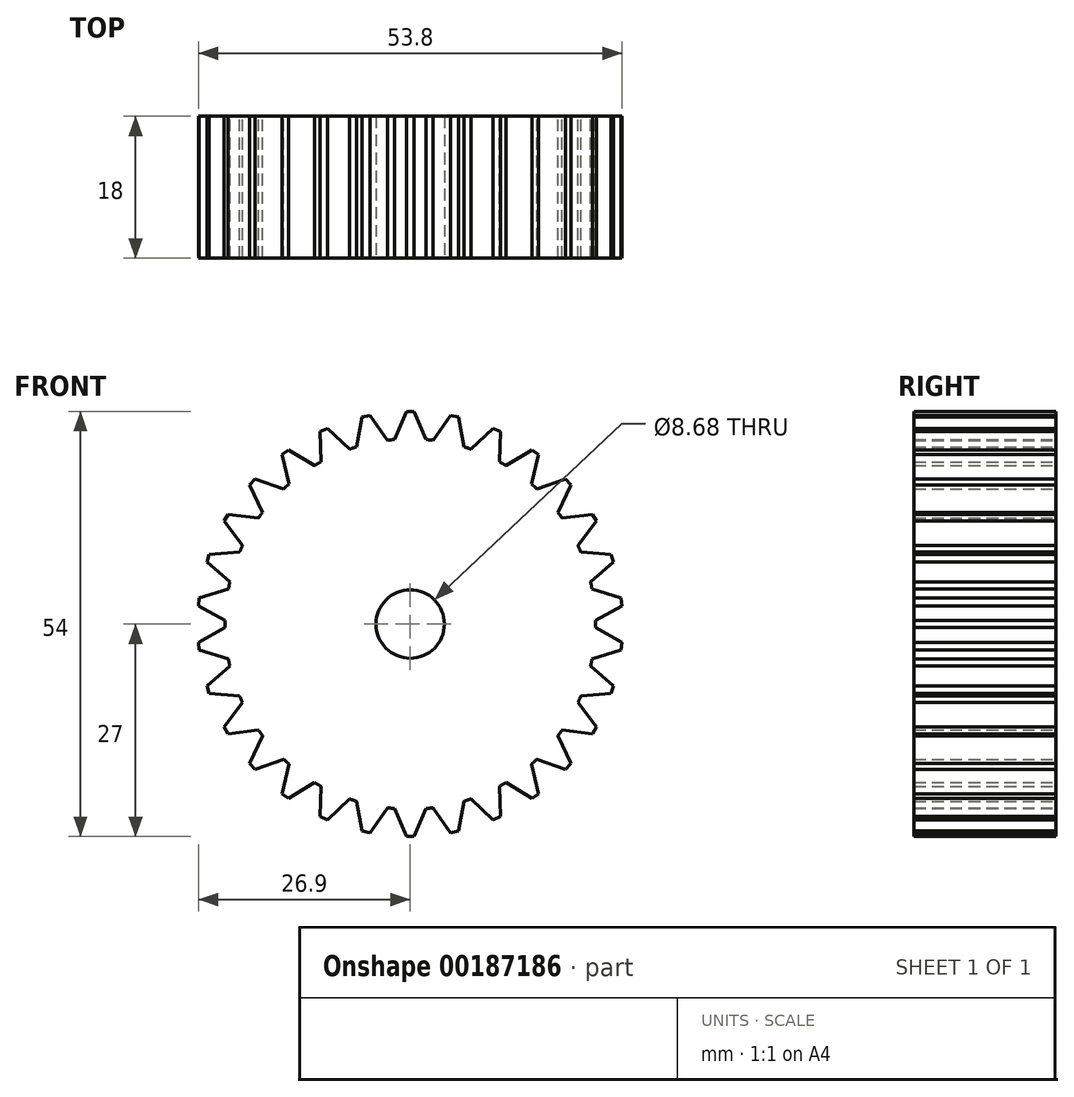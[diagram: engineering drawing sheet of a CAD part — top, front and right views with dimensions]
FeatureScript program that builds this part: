
annotation { "Feature Type Name" : "Feature", "Feature Type Description" : "" }
export const myFeature = defineFeature(function(context is Context, id is Id, definition is map)
    precondition{}
    {
        {
            var Q0;
            Q0=qCreatedBy(makeId("Front.planeOp"),FACE);
            var sketch = newSketch(context, id + "F0", { "sketchPlane" : qUnion([Q0])});
            skLineSegment(sketch, "E0", {"start": v(0, 0) * mm, "end": v(0, 27) * mm, "construction": true});
            skLineSegment(sketch, "E1", {"start": v(-0.5, 27) * mm, "end": v(0.5, 27) * mm, "construction": true});
            skLineSegment(sketch, "E2", {"start": v(0, 27) * mm, "end": v(0, 23.75) * mm, "construction": true});
            skPoint(sketch, "E3.startSnap0", {"position": v(0, 31.5) * mm});
            skLineSegment(sketch, "E4", {"start": v(-0.5, 27) * mm, "end": v(0, 27) * mm});
            skLineSegment(sketch, "E5.MirrorCS", {"start": v(0.5, 27) * mm, "end": v(0, 27) * mm});
            skLineSegment(sketch, "E6.MirrorCS", {"start": v(0.5, 27) * mm, "end": v(-0.5, 27) * mm, "construction": true});
            skCircle(sketch, "E7", {"center": v(0, 0) * mm, "radius": 23.52 * mm});
            skLineSegment(sketch, "E8", {"start": v(0.5, 27) * mm, "end": v(2, 23.44) * mm});
            skLineSegment(sketch, "E9", {"start": v(-0.5, 27) * mm, "end": v(-2, 23.44) * mm});
            skPoint(sketch, "E10.1.0", {"position": v(-6.55, 30.81) * mm});
            skLineSegment(sketch, "E10.1.1", {"start": v(-5.12, 26.51) * mm, "end": v(-2.92, 23.34) * mm});
            skLineSegment(sketch, "E10.1.2", {"start": v(-5.61, 26.4) * mm, "end": v(-4.94, 23.23) * mm, "construction": true});
            skLineSegment(sketch, "E10.1.3", {"start": v(-6.1, 26.3) * mm, "end": v(-6.83, 22.5) * mm});
            skPoint(sketch, "E10.1.4", {"position": v(-6.55, 30.81) * mm});
            skLineSegment(sketch, "E10.1.5", {"start": v(-5.12, 26.51) * mm, "end": v(-6.1, 26.3) * mm, "construction": true});
            skLineSegment(sketch, "E10.1.6", {"start": v(-6.1, 26.3) * mm, "end": v(-5.12, 26.51) * mm, "construction": true});
            skLineSegment(sketch, "E10.1.7", {"start": v(-5.12, 26.51) * mm, "end": v(-5.61, 26.4) * mm});
            skLineSegment(sketch, "E10.1.8", {"start": v(-6.1, 26.3) * mm, "end": v(-5.61, 26.4) * mm});
            skPoint(sketch, "E10.2.0", {"position": v(-12.81, 28.78) * mm});
            skLineSegment(sketch, "E10.2.1", {"start": v(-10.53, 24.87) * mm, "end": v(-7.7, 22.22) * mm});
            skLineSegment(sketch, "E10.2.2", {"start": v(-10.98, 24.67) * mm, "end": v(-9.66, 21.7) * mm, "construction": true});
            skLineSegment(sketch, "E10.2.3", {"start": v(-11.44, 24.46) * mm, "end": v(-11.36, 20.6) * mm});
            skPoint(sketch, "E10.2.4", {"position": v(-12.81, 28.78) * mm});
            skLineSegment(sketch, "E10.2.5", {"start": v(-10.53, 24.87) * mm, "end": v(-11.44, 24.46) * mm, "construction": true});
            skLineSegment(sketch, "E10.2.6", {"start": v(-11.44, 24.46) * mm, "end": v(-10.53, 24.87) * mm, "construction": true});
            skLineSegment(sketch, "E10.2.7", {"start": v(-10.53, 24.87) * mm, "end": v(-10.98, 24.67) * mm});
            skLineSegment(sketch, "E10.2.8", {"start": v(-11.44, 24.46) * mm, "end": v(-10.98, 24.67) * mm});
            skPoint(sketch, "E10.3.0", {"position": v(-18.52, 25.48) * mm});
            skLineSegment(sketch, "E10.3.1", {"start": v(-15.47, 22.14) * mm, "end": v(-12.16, 20.14) * mm});
            skLineSegment(sketch, "E10.3.2", {"start": v(-15.87, 21.84) * mm, "end": v(-13.96, 19.21) * mm, "construction": true});
            skLineSegment(sketch, "E10.3.3", {"start": v(-16.27, 21.55) * mm, "end": v(-15.4, 17.79) * mm});
            skPoint(sketch, "E10.3.4", {"position": v(-18.52, 25.48) * mm});
            skLineSegment(sketch, "E10.3.5", {"start": v(-15.47, 22.14) * mm, "end": v(-16.27, 21.55) * mm, "construction": true});
            skLineSegment(sketch, "E10.3.6", {"start": v(-16.27, 21.55) * mm, "end": v(-15.47, 22.14) * mm, "construction": true});
            skLineSegment(sketch, "E10.3.7", {"start": v(-15.47, 22.14) * mm, "end": v(-15.87, 21.84) * mm});
            skLineSegment(sketch, "E10.3.8", {"start": v(-16.27, 21.55) * mm, "end": v(-15.87, 21.84) * mm});
            skPoint(sketch, "E10.4.0", {"position": v(-23.4, 21.08) * mm});
            skLineSegment(sketch, "E10.4.1", {"start": v(-19.73, 18.44) * mm, "end": v(-16.08, 17.17) * mm});
            skLineSegment(sketch, "E10.4.2", {"start": v(-20.06, 18.07) * mm, "end": v(-17.65, 15.9) * mm, "construction": true});
            skLineSegment(sketch, "E10.4.3", {"start": v(-20.4, 17.7) * mm, "end": v(-18.76, 14.2) * mm});
            skPoint(sketch, "E10.4.4", {"position": v(-23.4, 21.08) * mm});
            skLineSegment(sketch, "E10.4.5", {"start": v(-19.73, 18.44) * mm, "end": v(-20.4, 17.7) * mm, "construction": true});
            skLineSegment(sketch, "E10.4.6", {"start": v(-20.4, 17.7) * mm, "end": v(-19.73, 18.44) * mm, "construction": true});
            skLineSegment(sketch, "E10.4.7", {"start": v(-19.73, 18.44) * mm, "end": v(-20.06, 18.07) * mm});
            skLineSegment(sketch, "E10.4.8", {"start": v(-20.4, 17.7) * mm, "end": v(-20.06, 18.07) * mm});
            skPoint(sketch, "E10.5.0", {"position": v(-27.28, 15.75) * mm});
            skLineSegment(sketch, "E10.5.1", {"start": v(-23.13, 13.93) * mm, "end": v(-19.3, 13.45) * mm});
            skLineSegment(sketch, "E10.5.2", {"start": v(-23.38, 13.5) * mm, "end": v(-20.57, 11.88) * mm, "construction": true});
            skLineSegment(sketch, "E10.5.3", {"start": v(-23.63, 13.07) * mm, "end": v(-21.3, 9.99) * mm});
            skPoint(sketch, "E10.5.4", {"position": v(-27.28, 15.75) * mm});
            skLineSegment(sketch, "E10.5.5", {"start": v(-23.13, 13.93) * mm, "end": v(-23.63, 13.07) * mm, "construction": true});
            skLineSegment(sketch, "E10.5.6", {"start": v(-23.63, 13.07) * mm, "end": v(-23.13, 13.93) * mm, "construction": true});
            skLineSegment(sketch, "E10.5.7", {"start": v(-23.13, 13.93) * mm, "end": v(-23.38, 13.5) * mm});
            skLineSegment(sketch, "E10.5.8", {"start": v(-23.63, 13.07) * mm, "end": v(-23.38, 13.5) * mm});
            skPoint(sketch, "E10.6.0", {"position": v(-29.96, 9.73) * mm});
            skLineSegment(sketch, "E10.6.1", {"start": v(-25.52, 8.82) * mm, "end": v(-21.67, 9.14) * mm});
            skLineSegment(sketch, "E10.6.2", {"start": v(-25.68, 8.34) * mm, "end": v(-22.59, 7.34) * mm, "construction": true});
            skLineSegment(sketch, "E10.6.3", {"start": v(-25.83, 7.87) * mm, "end": v(-22.9, 5.34) * mm});
            skPoint(sketch, "E10.6.4", {"position": v(-29.96, 9.73) * mm});
            skLineSegment(sketch, "E10.6.5", {"start": v(-25.52, 8.82) * mm, "end": v(-25.83, 7.87) * mm, "construction": true});
            skLineSegment(sketch, "E10.6.6", {"start": v(-25.83, 7.87) * mm, "end": v(-25.52, 8.82) * mm, "construction": true});
            skLineSegment(sketch, "E10.6.7", {"start": v(-25.52, 8.82) * mm, "end": v(-25.68, 8.34) * mm});
            skLineSegment(sketch, "E10.6.8", {"start": v(-25.83, 7.87) * mm, "end": v(-25.68, 8.34) * mm});
            skPoint(sketch, "E10.7.0", {"position": v(-31.33, 3.3) * mm});
            skLineSegment(sketch, "E10.7.1", {"start": v(-26.8, 3.32) * mm, "end": v(-23.1, 4.44) * mm});
            skLineSegment(sketch, "E10.7.2", {"start": v(-26.85, 2.82) * mm, "end": v(-23.62, 2.48) * mm, "construction": true});
            skLineSegment(sketch, "E10.7.3", {"start": v(-26.9, 2.33) * mm, "end": v(-23.52, 0.46) * mm});
            skPoint(sketch, "E10.7.4", {"position": v(-31.33, 3.3) * mm});
            skLineSegment(sketch, "E10.7.5", {"start": v(-26.8, 3.32) * mm, "end": v(-26.9, 2.33) * mm, "construction": true});
            skLineSegment(sketch, "E10.7.6", {"start": v(-26.9, 2.33) * mm, "end": v(-26.8, 3.32) * mm, "construction": true});
            skLineSegment(sketch, "E10.7.7", {"start": v(-26.8, 3.32) * mm, "end": v(-26.85, 2.82) * mm});
            skLineSegment(sketch, "E10.7.8", {"start": v(-26.9, 2.33) * mm, "end": v(-26.85, 2.82) * mm});
            skPoint(sketch, "E10.8.0", {"position": v(-31.33, -3.3) * mm});
            skLineSegment(sketch, "E10.8.1", {"start": v(-26.9, -2.33) * mm, "end": v(-23.52, -0.46) * mm});
            skLineSegment(sketch, "E10.8.2", {"start": v(-26.85, -2.82) * mm, "end": v(-23.62, -2.48) * mm, "construction": true});
            skLineSegment(sketch, "E10.8.3", {"start": v(-26.8, -3.32) * mm, "end": v(-23.1, -4.44) * mm});
            skPoint(sketch, "E10.8.4", {"position": v(-31.33, -3.3) * mm});
            skLineSegment(sketch, "E10.8.5", {"start": v(-26.9, -2.33) * mm, "end": v(-26.8, -3.32) * mm, "construction": true});
            skLineSegment(sketch, "E10.8.6", {"start": v(-26.8, -3.32) * mm, "end": v(-26.9, -2.33) * mm, "construction": true});
            skLineSegment(sketch, "E10.8.7", {"start": v(-26.9, -2.33) * mm, "end": v(-26.85, -2.82) * mm});
            skLineSegment(sketch, "E10.8.8", {"start": v(-26.8, -3.32) * mm, "end": v(-26.85, -2.82) * mm});
            skPoint(sketch, "E10.9.0", {"position": v(-29.96, -9.73) * mm});
            skLineSegment(sketch, "E10.9.1", {"start": v(-25.83, -7.87) * mm, "end": v(-22.9, -5.34) * mm});
            skLineSegment(sketch, "E10.9.2", {"start": v(-25.68, -8.34) * mm, "end": v(-22.59, -7.34) * mm, "construction": true});
            skLineSegment(sketch, "E10.9.3", {"start": v(-25.52, -8.82) * mm, "end": v(-21.67, -9.14) * mm});
            skPoint(sketch, "E10.9.4", {"position": v(-29.96, -9.73) * mm});
            skLineSegment(sketch, "E10.9.5", {"start": v(-25.83, -7.87) * mm, "end": v(-25.52, -8.82) * mm, "construction": true});
            skLineSegment(sketch, "E10.9.6", {"start": v(-25.52, -8.82) * mm, "end": v(-25.83, -7.87) * mm, "construction": true});
            skLineSegment(sketch, "E10.9.7", {"start": v(-25.83, -7.87) * mm, "end": v(-25.68, -8.34) * mm});
            skLineSegment(sketch, "E10.9.8", {"start": v(-25.52, -8.82) * mm, "end": v(-25.68, -8.34) * mm});
            skPoint(sketch, "E10.10.0", {"position": v(-27.28, -15.75) * mm});
            skLineSegment(sketch, "E10.10.1", {"start": v(-23.63, -13.07) * mm, "end": v(-21.3, -9.99) * mm});
            skLineSegment(sketch, "E10.10.2", {"start": v(-23.38, -13.5) * mm, "end": v(-20.57, -11.87) * mm, "construction": true});
            skLineSegment(sketch, "E10.10.3", {"start": v(-23.13, -13.93) * mm, "end": v(-19.3, -13.45) * mm});
            skPoint(sketch, "E10.10.4", {"position": v(-27.28, -15.75) * mm});
            skLineSegment(sketch, "E10.10.5", {"start": v(-23.63, -13.07) * mm, "end": v(-23.13, -13.93) * mm, "construction": true});
            skLineSegment(sketch, "E10.10.6", {"start": v(-23.13, -13.93) * mm, "end": v(-23.63, -13.07) * mm, "construction": true});
            skLineSegment(sketch, "E10.10.7", {"start": v(-23.63, -13.07) * mm, "end": v(-23.38, -13.5) * mm});
            skLineSegment(sketch, "E10.10.8", {"start": v(-23.13, -13.93) * mm, "end": v(-23.38, -13.5) * mm});
            skPoint(sketch, "E10.11.0", {"position": v(-23.4, -21.08) * mm});
            skLineSegment(sketch, "E10.11.1", {"start": v(-20.4, -17.7) * mm, "end": v(-18.76, -14.2) * mm});
            skLineSegment(sketch, "E10.11.2", {"start": v(-20.06, -18.07) * mm, "end": v(-17.65, -15.9) * mm, "construction": true});
            skLineSegment(sketch, "E10.11.3", {"start": v(-19.73, -18.44) * mm, "end": v(-16.08, -17.17) * mm});
            skPoint(sketch, "E10.11.4", {"position": v(-23.4, -21.08) * mm});
            skLineSegment(sketch, "E10.11.5", {"start": v(-20.4, -17.7) * mm, "end": v(-19.73, -18.44) * mm, "construction": true});
            skLineSegment(sketch, "E10.11.6", {"start": v(-19.73, -18.44) * mm, "end": v(-20.4, -17.7) * mm, "construction": true});
            skLineSegment(sketch, "E10.11.7", {"start": v(-20.4, -17.7) * mm, "end": v(-20.06, -18.07) * mm});
            skLineSegment(sketch, "E10.11.8", {"start": v(-19.73, -18.44) * mm, "end": v(-20.06, -18.07) * mm});
            skLineSegment(sketch, "E11.1.12.0", {"start": v(-16.27, -21.55) * mm, "end": v(-15.4, -17.79) * mm});
            skLineSegment(sketch, "E11.4.12.0", {"start": v(-15.87, -21.84) * mm, "end": v(-13.96, -19.21) * mm, "construction": true});
            skLineSegment(sketch, "E11.7.12.0", {"start": v(-15.47, -22.14) * mm, "end": v(-12.16, -20.14) * mm});
            skPoint(sketch, "E11.9.12.0", {"position": v(-18.52, -25.48) * mm});
            skPoint(sketch, "E11.10.12.0", {"position": v(-18.52, -25.48) * mm});
            skLineSegment(sketch, "E11.11.12.0", {"start": v(-16.27, -21.55) * mm, "end": v(-15.47, -22.14) * mm, "construction": true});
            skLineSegment(sketch, "E11.14.12.0", {"start": v(-15.47, -22.14) * mm, "end": v(-16.27, -21.55) * mm, "construction": true});
            skLineSegment(sketch, "E11.17.12.0", {"start": v(-16.27, -21.55) * mm, "end": v(-15.87, -21.84) * mm});
            skLineSegment(sketch, "E11.20.12.0", {"start": v(-15.47, -22.14) * mm, "end": v(-15.87, -21.84) * mm});
            skLineSegment(sketch, "E11.1.13.0", {"start": v(-11.44, -24.46) * mm, "end": v(-11.36, -20.6) * mm});
            skLineSegment(sketch, "E11.4.13.0", {"start": v(-10.98, -24.67) * mm, "end": v(-9.66, -21.7) * mm, "construction": true});
            skLineSegment(sketch, "E11.7.13.0", {"start": v(-10.53, -24.87) * mm, "end": v(-7.7, -22.22) * mm});
            skPoint(sketch, "E11.9.13.0", {"position": v(-12.81, -28.78) * mm});
            skPoint(sketch, "E11.10.13.0", {"position": v(-12.81, -28.78) * mm});
            skLineSegment(sketch, "E11.11.13.0", {"start": v(-11.44, -24.46) * mm, "end": v(-10.53, -24.87) * mm, "construction": true});
            skLineSegment(sketch, "E11.14.13.0", {"start": v(-10.53, -24.87) * mm, "end": v(-11.44, -24.46) * mm, "construction": true});
            skLineSegment(sketch, "E11.17.13.0", {"start": v(-11.44, -24.46) * mm, "end": v(-10.98, -24.67) * mm});
            skLineSegment(sketch, "E11.20.13.0", {"start": v(-10.53, -24.87) * mm, "end": v(-10.98, -24.67) * mm});
            skLineSegment(sketch, "E11.1.14.0", {"start": v(-6.1, -26.3) * mm, "end": v(-6.83, -22.5) * mm});
            skLineSegment(sketch, "E11.4.14.0", {"start": v(-5.61, -26.4) * mm, "end": v(-4.94, -23.23) * mm, "construction": true});
            skLineSegment(sketch, "E11.7.14.0", {"start": v(-5.12, -26.51) * mm, "end": v(-2.92, -23.34) * mm});
            skPoint(sketch, "E11.9.14.0", {"position": v(-6.55, -30.81) * mm});
            skPoint(sketch, "E11.10.14.0", {"position": v(-6.55, -30.81) * mm});
            skLineSegment(sketch, "E11.11.14.0", {"start": v(-6.1, -26.3) * mm, "end": v(-5.12, -26.51) * mm, "construction": true});
            skLineSegment(sketch, "E11.14.14.0", {"start": v(-5.12, -26.51) * mm, "end": v(-6.1, -26.3) * mm, "construction": true});
            skLineSegment(sketch, "E11.17.14.0", {"start": v(-6.1, -26.3) * mm, "end": v(-5.61, -26.4) * mm});
            skLineSegment(sketch, "E11.20.14.0", {"start": v(-5.12, -26.51) * mm, "end": v(-5.61, -26.4) * mm});
            skLineSegment(sketch, "E11.1.15.0", {"start": v(-0.5, -27) * mm, "end": v(-2, -23.44) * mm});
            skLineSegment(sketch, "E11.4.15.0", {"start": v(0, -27) * mm, "end": v(0, -23.75) * mm, "construction": true});
            skLineSegment(sketch, "E11.7.15.0", {"start": v(0.5, -27) * mm, "end": v(2, -23.44) * mm});
            skPoint(sketch, "E11.9.15.0", {"position": v(0, -31.5) * mm});
            skPoint(sketch, "E11.10.15.0", {"position": v(0, -31.5) * mm});
            skLineSegment(sketch, "E11.11.15.0", {"start": v(-0.5, -27) * mm, "end": v(0.5, -27) * mm, "construction": true});
            skLineSegment(sketch, "E11.14.15.0", {"start": v(0.5, -27) * mm, "end": v(-0.5, -27) * mm, "construction": true});
            skLineSegment(sketch, "E11.17.15.0", {"start": v(-0.5, -27) * mm, "end": v(0, -27) * mm});
            skLineSegment(sketch, "E11.20.15.0", {"start": v(0.5, -27) * mm, "end": v(0, -27) * mm});
            skLineSegment(sketch, "E11.1.16.0", {"start": v(5.12, -26.51) * mm, "end": v(2.92, -23.34) * mm});
            skLineSegment(sketch, "E11.4.16.0", {"start": v(5.61, -26.4) * mm, "end": v(4.94, -23.23) * mm, "construction": true});
            skLineSegment(sketch, "E11.7.16.0", {"start": v(6.1, -26.3) * mm, "end": v(6.83, -22.5) * mm});
            skPoint(sketch, "E11.9.16.0", {"position": v(6.55, -30.81) * mm});
            skPoint(sketch, "E11.10.16.0", {"position": v(6.55, -30.81) * mm});
            skLineSegment(sketch, "E11.11.16.0", {"start": v(5.12, -26.51) * mm, "end": v(6.1, -26.3) * mm, "construction": true});
            skLineSegment(sketch, "E11.14.16.0", {"start": v(6.1, -26.3) * mm, "end": v(5.12, -26.51) * mm, "construction": true});
            skLineSegment(sketch, "E11.17.16.0", {"start": v(5.12, -26.51) * mm, "end": v(5.61, -26.4) * mm});
            skLineSegment(sketch, "E11.20.16.0", {"start": v(6.1, -26.3) * mm, "end": v(5.61, -26.4) * mm});
            skLineSegment(sketch, "E11.1.17.0", {"start": v(10.53, -24.87) * mm, "end": v(7.7, -22.22) * mm});
            skLineSegment(sketch, "E11.4.17.0", {"start": v(10.98, -24.67) * mm, "end": v(9.66, -21.7) * mm, "construction": true});
            skLineSegment(sketch, "E11.7.17.0", {"start": v(11.44, -24.46) * mm, "end": v(11.36, -20.6) * mm});
            skPoint(sketch, "E11.9.17.0", {"position": v(12.81, -28.78) * mm});
            skPoint(sketch, "E11.10.17.0", {"position": v(12.81, -28.78) * mm});
            skLineSegment(sketch, "E11.11.17.0", {"start": v(10.53, -24.87) * mm, "end": v(11.44, -24.46) * mm, "construction": true});
            skLineSegment(sketch, "E11.14.17.0", {"start": v(11.44, -24.46) * mm, "end": v(10.53, -24.87) * mm, "construction": true});
            skLineSegment(sketch, "E11.17.17.0", {"start": v(10.53, -24.87) * mm, "end": v(10.98, -24.67) * mm});
            skLineSegment(sketch, "E11.20.17.0", {"start": v(11.44, -24.46) * mm, "end": v(10.98, -24.67) * mm});
            skLineSegment(sketch, "E11.1.18.0", {"start": v(15.47, -22.14) * mm, "end": v(12.16, -20.14) * mm});
            skLineSegment(sketch, "E11.4.18.0", {"start": v(15.87, -21.84) * mm, "end": v(13.96, -19.21) * mm, "construction": true});
            skLineSegment(sketch, "E11.7.18.0", {"start": v(16.27, -21.55) * mm, "end": v(15.4, -17.79) * mm});
            skPoint(sketch, "E11.9.18.0", {"position": v(18.52, -25.48) * mm});
            skPoint(sketch, "E11.10.18.0", {"position": v(18.52, -25.48) * mm});
            skLineSegment(sketch, "E11.11.18.0", {"start": v(15.47, -22.14) * mm, "end": v(16.27, -21.55) * mm, "construction": true});
            skLineSegment(sketch, "E11.14.18.0", {"start": v(16.27, -21.55) * mm, "end": v(15.47, -22.14) * mm, "construction": true});
            skLineSegment(sketch, "E11.17.18.0", {"start": v(15.47, -22.14) * mm, "end": v(15.87, -21.84) * mm});
            skLineSegment(sketch, "E11.20.18.0", {"start": v(16.27, -21.55) * mm, "end": v(15.87, -21.84) * mm});
            skLineSegment(sketch, "E11.1.19.0", {"start": v(19.73, -18.44) * mm, "end": v(16.08, -17.17) * mm});
            skLineSegment(sketch, "E11.4.19.0", {"start": v(20.06, -18.07) * mm, "end": v(17.65, -15.9) * mm, "construction": true});
            skLineSegment(sketch, "E11.7.19.0", {"start": v(20.4, -17.7) * mm, "end": v(18.76, -14.2) * mm});
            skPoint(sketch, "E11.9.19.0", {"position": v(23.4, -21.08) * mm});
            skPoint(sketch, "E11.10.19.0", {"position": v(23.4, -21.08) * mm});
            skLineSegment(sketch, "E11.11.19.0", {"start": v(19.73, -18.44) * mm, "end": v(20.4, -17.7) * mm, "construction": true});
            skLineSegment(sketch, "E11.14.19.0", {"start": v(20.4, -17.7) * mm, "end": v(19.73, -18.44) * mm, "construction": true});
            skLineSegment(sketch, "E11.17.19.0", {"start": v(19.73, -18.44) * mm, "end": v(20.06, -18.07) * mm});
            skLineSegment(sketch, "E11.20.19.0", {"start": v(20.4, -17.7) * mm, "end": v(20.06, -18.07) * mm});
            skLineSegment(sketch, "E12.1.20.0", {"start": v(23.13, -13.93) * mm, "end": v(19.3, -13.45) * mm});
            skLineSegment(sketch, "E12.4.20.0", {"start": v(23.38, -13.5) * mm, "end": v(20.57, -11.88) * mm, "construction": true});
            skLineSegment(sketch, "E12.7.20.0", {"start": v(23.63, -13.07) * mm, "end": v(21.3, -9.99) * mm});
            skPoint(sketch, "E12.9.20.0", {"position": v(27.28, -15.75) * mm});
            skPoint(sketch, "E12.10.20.0", {"position": v(27.28, -15.75) * mm});
            skLineSegment(sketch, "E12.11.20.0", {"start": v(23.13, -13.93) * mm, "end": v(23.63, -13.07) * mm, "construction": true});
            skLineSegment(sketch, "E12.14.20.0", {"start": v(23.63, -13.07) * mm, "end": v(23.13, -13.93) * mm, "construction": true});
            skLineSegment(sketch, "E12.17.20.0", {"start": v(23.13, -13.93) * mm, "end": v(23.38, -13.5) * mm});
            skLineSegment(sketch, "E12.20.20.0", {"start": v(23.63, -13.07) * mm, "end": v(23.38, -13.5) * mm});
            skLineSegment(sketch, "E12.1.21.0", {"start": v(25.52, -8.82) * mm, "end": v(21.67, -9.14) * mm});
            skLineSegment(sketch, "E12.4.21.0", {"start": v(25.68, -8.34) * mm, "end": v(22.59, -7.34) * mm, "construction": true});
            skLineSegment(sketch, "E12.7.21.0", {"start": v(25.83, -7.87) * mm, "end": v(22.9, -5.34) * mm});
            skPoint(sketch, "E12.9.21.0", {"position": v(29.96, -9.73) * mm});
            skPoint(sketch, "E12.10.21.0", {"position": v(29.96, -9.73) * mm});
            skLineSegment(sketch, "E12.11.21.0", {"start": v(25.52, -8.82) * mm, "end": v(25.83, -7.87) * mm, "construction": true});
            skLineSegment(sketch, "E12.14.21.0", {"start": v(25.83, -7.87) * mm, "end": v(25.52, -8.82) * mm, "construction": true});
            skLineSegment(sketch, "E12.17.21.0", {"start": v(25.52, -8.82) * mm, "end": v(25.68, -8.34) * mm});
            skLineSegment(sketch, "E12.20.21.0", {"start": v(25.83, -7.87) * mm, "end": v(25.68, -8.34) * mm});
            skLineSegment(sketch, "E12.1.22.0", {"start": v(26.8, -3.32) * mm, "end": v(23.1, -4.44) * mm});
            skLineSegment(sketch, "E12.4.22.0", {"start": v(26.85, -2.82) * mm, "end": v(23.62, -2.48) * mm, "construction": true});
            skLineSegment(sketch, "E12.7.22.0", {"start": v(26.9, -2.33) * mm, "end": v(23.52, -0.46) * mm});
            skPoint(sketch, "E12.9.22.0", {"position": v(31.33, -3.3) * mm});
            skPoint(sketch, "E12.10.22.0", {"position": v(31.33, -3.3) * mm});
            skLineSegment(sketch, "E12.11.22.0", {"start": v(26.8, -3.32) * mm, "end": v(26.9, -2.33) * mm, "construction": true});
            skLineSegment(sketch, "E12.14.22.0", {"start": v(26.9, -2.33) * mm, "end": v(26.8, -3.32) * mm, "construction": true});
            skLineSegment(sketch, "E12.17.22.0", {"start": v(26.8, -3.32) * mm, "end": v(26.85, -2.82) * mm});
            skLineSegment(sketch, "E12.20.22.0", {"start": v(26.9, -2.33) * mm, "end": v(26.85, -2.82) * mm});
            skLineSegment(sketch, "E12.1.23.0", {"start": v(26.9, 2.33) * mm, "end": v(23.52, 0.46) * mm});
            skLineSegment(sketch, "E12.4.23.0", {"start": v(26.85, 2.82) * mm, "end": v(23.62, 2.48) * mm, "construction": true});
            skLineSegment(sketch, "E12.7.23.0", {"start": v(26.8, 3.32) * mm, "end": v(23.1, 4.44) * mm});
            skPoint(sketch, "E12.9.23.0", {"position": v(31.33, 3.3) * mm});
            skPoint(sketch, "E12.10.23.0", {"position": v(31.33, 3.3) * mm});
            skLineSegment(sketch, "E12.11.23.0", {"start": v(26.9, 2.33) * mm, "end": v(26.8, 3.32) * mm, "construction": true});
            skLineSegment(sketch, "E12.14.23.0", {"start": v(26.8, 3.32) * mm, "end": v(26.9, 2.33) * mm, "construction": true});
            skLineSegment(sketch, "E12.17.23.0", {"start": v(26.9, 2.33) * mm, "end": v(26.85, 2.82) * mm});
            skLineSegment(sketch, "E12.20.23.0", {"start": v(26.8, 3.32) * mm, "end": v(26.85, 2.82) * mm});
            skLineSegment(sketch, "E12.1.24.0", {"start": v(25.83, 7.87) * mm, "end": v(22.9, 5.34) * mm});
            skLineSegment(sketch, "E12.4.24.0", {"start": v(25.68, 8.34) * mm, "end": v(22.59, 7.34) * mm, "construction": true});
            skLineSegment(sketch, "E12.7.24.0", {"start": v(25.52, 8.82) * mm, "end": v(21.67, 9.14) * mm});
            skPoint(sketch, "E12.9.24.0", {"position": v(29.96, 9.73) * mm});
            skPoint(sketch, "E12.10.24.0", {"position": v(29.96, 9.73) * mm});
            skLineSegment(sketch, "E12.11.24.0", {"start": v(25.83, 7.87) * mm, "end": v(25.52, 8.82) * mm, "construction": true});
            skLineSegment(sketch, "E12.14.24.0", {"start": v(25.52, 8.82) * mm, "end": v(25.83, 7.87) * mm, "construction": true});
            skLineSegment(sketch, "E12.17.24.0", {"start": v(25.83, 7.87) * mm, "end": v(25.68, 8.34) * mm});
            skLineSegment(sketch, "E12.20.24.0", {"start": v(25.52, 8.82) * mm, "end": v(25.68, 8.34) * mm});
            skLineSegment(sketch, "E13.1.25.0", {"start": v(23.63, 13.07) * mm, "end": v(21.3, 9.99) * mm});
            skLineSegment(sketch, "E13.4.25.0", {"start": v(23.38, 13.5) * mm, "end": v(20.57, 11.88) * mm, "construction": true});
            skLineSegment(sketch, "E13.7.25.0", {"start": v(23.13, 13.93) * mm, "end": v(19.3, 13.45) * mm});
            skPoint(sketch, "E13.9.25.0", {"position": v(27.28, 15.75) * mm});
            skPoint(sketch, "E13.10.25.0", {"position": v(27.28, 15.75) * mm});
            skLineSegment(sketch, "E13.11.25.0", {"start": v(23.63, 13.07) * mm, "end": v(23.13, 13.93) * mm, "construction": true});
            skLineSegment(sketch, "E13.14.25.0", {"start": v(23.13, 13.93) * mm, "end": v(23.63, 13.07) * mm, "construction": true});
            skLineSegment(sketch, "E13.17.25.0", {"start": v(23.63, 13.07) * mm, "end": v(23.38, 13.5) * mm});
            skLineSegment(sketch, "E13.20.25.0", {"start": v(23.13, 13.93) * mm, "end": v(23.38, 13.5) * mm});
            skLineSegment(sketch, "E13.1.26.0", {"start": v(20.4, 17.7) * mm, "end": v(18.76, 14.2) * mm});
            skLineSegment(sketch, "E13.4.26.0", {"start": v(20.06, 18.07) * mm, "end": v(17.65, 15.9) * mm, "construction": true});
            skLineSegment(sketch, "E13.7.26.0", {"start": v(19.73, 18.44) * mm, "end": v(16.08, 17.17) * mm});
            skPoint(sketch, "E13.9.26.0", {"position": v(23.4, 21.08) * mm});
            skPoint(sketch, "E13.10.26.0", {"position": v(23.4, 21.08) * mm});
            skLineSegment(sketch, "E13.11.26.0", {"start": v(20.4, 17.7) * mm, "end": v(19.73, 18.44) * mm, "construction": true});
            skLineSegment(sketch, "E13.14.26.0", {"start": v(19.73, 18.44) * mm, "end": v(20.4, 17.7) * mm, "construction": true});
            skLineSegment(sketch, "E13.17.26.0", {"start": v(20.4, 17.7) * mm, "end": v(20.06, 18.07) * mm});
            skLineSegment(sketch, "E13.20.26.0", {"start": v(19.73, 18.44) * mm, "end": v(20.06, 18.07) * mm});
            skLineSegment(sketch, "E13.1.27.0", {"start": v(16.27, 21.55) * mm, "end": v(15.4, 17.79) * mm});
            skLineSegment(sketch, "E13.4.27.0", {"start": v(15.87, 21.84) * mm, "end": v(13.96, 19.21) * mm, "construction": true});
            skLineSegment(sketch, "E13.7.27.0", {"start": v(15.47, 22.14) * mm, "end": v(12.16, 20.14) * mm});
            skPoint(sketch, "E13.9.27.0", {"position": v(18.52, 25.48) * mm});
            skPoint(sketch, "E13.10.27.0", {"position": v(18.52, 25.48) * mm});
            skLineSegment(sketch, "E13.11.27.0", {"start": v(16.27, 21.55) * mm, "end": v(15.47, 22.14) * mm, "construction": true});
            skLineSegment(sketch, "E13.14.27.0", {"start": v(15.47, 22.14) * mm, "end": v(16.27, 21.55) * mm, "construction": true});
            skLineSegment(sketch, "E13.17.27.0", {"start": v(16.27, 21.55) * mm, "end": v(15.87, 21.84) * mm});
            skLineSegment(sketch, "E13.20.27.0", {"start": v(15.47, 22.14) * mm, "end": v(15.87, 21.84) * mm});
            skLineSegment(sketch, "E14.1.28.0", {"start": v(11.44, 24.46) * mm, "end": v(11.36, 20.6) * mm});
            skLineSegment(sketch, "E14.4.28.0", {"start": v(10.98, 24.67) * mm, "end": v(9.66, 21.7) * mm, "construction": true});
            skLineSegment(sketch, "E14.7.28.0", {"start": v(10.53, 24.87) * mm, "end": v(7.7, 22.22) * mm});
            skPoint(sketch, "E14.9.28.0", {"position": v(12.81, 28.78) * mm});
            skPoint(sketch, "E14.10.28.0", {"position": v(12.81, 28.78) * mm});
            skLineSegment(sketch, "E14.11.28.0", {"start": v(11.44, 24.46) * mm, "end": v(10.53, 24.87) * mm, "construction": true});
            skLineSegment(sketch, "E14.14.28.0", {"start": v(10.53, 24.87) * mm, "end": v(11.44, 24.46) * mm, "construction": true});
            skLineSegment(sketch, "E14.17.28.0", {"start": v(11.44, 24.46) * mm, "end": v(10.98, 24.67) * mm});
            skLineSegment(sketch, "E14.20.28.0", {"start": v(10.53, 24.87) * mm, "end": v(10.98, 24.67) * mm});
            skLineSegment(sketch, "E14.1.29.0", {"start": v(6.1, 26.3) * mm, "end": v(6.83, 22.5) * mm});
            skLineSegment(sketch, "E14.4.29.0", {"start": v(5.61, 26.4) * mm, "end": v(4.94, 23.23) * mm, "construction": true});
            skLineSegment(sketch, "E14.7.29.0", {"start": v(5.12, 26.51) * mm, "end": v(2.92, 23.34) * mm});
            skPoint(sketch, "E14.9.29.0", {"position": v(6.55, 30.81) * mm});
            skPoint(sketch, "E14.10.29.0", {"position": v(6.55, 30.81) * mm});
            skLineSegment(sketch, "E14.11.29.0", {"start": v(6.1, 26.3) * mm, "end": v(5.12, 26.51) * mm, "construction": true});
            skLineSegment(sketch, "E14.14.29.0", {"start": v(5.12, 26.51) * mm, "end": v(6.1, 26.3) * mm, "construction": true});
            skLineSegment(sketch, "E14.17.29.0", {"start": v(6.1, 26.3) * mm, "end": v(5.61, 26.4) * mm});
            skLineSegment(sketch, "E14.20.29.0", {"start": v(5.12, 26.51) * mm, "end": v(5.61, 26.4) * mm});
            skSolve(sketch);
        }
        {
            var Q0;
            Q0=qSketchRegion(id+"F0",true);
            extrude(context, id + "F1", {"entities" : qUnion([Q0]), "depth" : 18 * mm});
        }
        {
            var Q0;
            Q0=makeQuery(id+"F1.opExtrude","CAP_FACE",FACE,{"disambiguationData":[OSD([sQuery(id+"F0.wireOp",EDGE,"E4"),sQuery(id+"F0.wireOp",EDGE,"E5.MirrorCS"),sQuery(id+"F0.wireOp",EDGE,"E7"),sQuery(id+"F0.wireOp",EDGE,"E8"),sQuery(id+"F0.wireOp",EDGE,"E9"),sQuery(id+"F0.wireOp",EDGE,"E10.1.1"),sQuery(id+"F0.wireOp",EDGE,"E10.1.3"),sQuery(id+"F0.wireOp",EDGE,"E10.1.7"),sQuery(id+"F0.wireOp",EDGE,"E10.1.8"),sQuery(id+"F0.wireOp",EDGE,"E10.2.1"),sQuery(id+"F0.wireOp",EDGE,"E10.2.3"),sQuery(id+"F0.wireOp",EDGE,"E10.2.7"),sQuery(id+"F0.wireOp",EDGE,"E10.2.8"),sQuery(id+"F0.wireOp",EDGE,"E10.3.1"),sQuery(id+"F0.wireOp",EDGE,"E10.3.3"),sQuery(id+"F0.wireOp",EDGE,"E10.3.7"),sQuery(id+"F0.wireOp",EDGE,"E10.3.8"),sQuery(id+"F0.wireOp",EDGE,"E10.4.1"),sQuery(id+"F0.wireOp",EDGE,"E10.4.3"),sQuery(id+"F0.wireOp",EDGE,"E10.4.7"),sQuery(id+"F0.wireOp",EDGE,"E10.4.8"),sQuery(id+"F0.wireOp",EDGE,"E10.5.1"),sQuery(id+"F0.wireOp",EDGE,"E10.5.3"),sQuery(id+"F0.wireOp",EDGE,"E10.5.7"),sQuery(id+"F0.wireOp",EDGE,"E10.5.8"),sQuery(id+"F0.wireOp",EDGE,"E10.6.1"),sQuery(id+"F0.wireOp",EDGE,"E10.6.3"),sQuery(id+"F0.wireOp",EDGE,"E10.6.7"),sQuery(id+"F0.wireOp",EDGE,"E10.6.8"),sQuery(id+"F0.wireOp",EDGE,"E10.7.1"),sQuery(id+"F0.wireOp",EDGE,"E10.7.3"),sQuery(id+"F0.wireOp",EDGE,"E10.7.7"),sQuery(id+"F0.wireOp",EDGE,"E10.7.8"),sQuery(id+"F0.wireOp",EDGE,"E10.8.1"),sQuery(id+"F0.wireOp",EDGE,"E10.8.3"),sQuery(id+"F0.wireOp",EDGE,"E10.8.7"),sQuery(id+"F0.wireOp",EDGE,"E10.8.8"),sQuery(id+"F0.wireOp",EDGE,"E10.9.1"),sQuery(id+"F0.wireOp",EDGE,"E10.9.3"),sQuery(id+"F0.wireOp",EDGE,"E10.9.7"),sQuery(id+"F0.wireOp",EDGE,"E10.9.8"),sQuery(id+"F0.wireOp",EDGE,"E10.10.1"),sQuery(id+"F0.wireOp",EDGE,"E10.10.3"),sQuery(id+"F0.wireOp",EDGE,"E10.10.7"),sQuery(id+"F0.wireOp",EDGE,"E10.10.8"),sQuery(id+"F0.wireOp",EDGE,"E10.11.1"),sQuery(id+"F0.wireOp",EDGE,"E10.11.3"),sQuery(id+"F0.wireOp",EDGE,"E10.11.7"),sQuery(id+"F0.wireOp",EDGE,"E10.11.8")])],"isStart":true});
            var sketch = newSketch(context, id + "F2", { "sketchPlane" : qUnion([Q0])});
            skArc(sketch, "E15", {"start": v(-2, -2.24) * mm, "mid": v(0, -3) * mm, "end": v(2, -2.24) * mm});
            skLineSegment(sketch, "E16.left", {"start": v(-2, 2.24) * mm, "end": v(-2, -2.24) * mm});
            skLineSegment(sketch, "E16.right", {"start": v(2, 2.24) * mm, "end": v(2, -2.24) * mm});
            skPoint(sketch, "E17.orphan", {"position": v(-2, 2.5) * mm});
            skPoint(sketch, "E18.trimOffspring.end.orphan", {"position": v(2, 2.5) * mm});
            skPoint(sketch, "E19.orphan", {"position": v(-2, -2.5) * mm});
            skPoint(sketch, "E20.orphan", {"position": v(2, -2.5) * mm});
            skArc(sketch, "E21.trimOffspring", {"start": v(2, 2.24) * mm, "mid": v(0, 3) * mm, "end": v(-2, 2.24) * mm});
            skSolve(sketch);
        }
        {
            var Q0;
            Q0=qSketchRegion(id+"F2",true);
            extrude(context, id + "F3", {"entities" : qUnion([Q0]), "operationType" : NewBodyOperationType.REMOVE, "oppositeDirection" : true, "depth" : 9 * mm});
        }
        {
            var Q0;
            Q0=makeQuery(id+"F1.opExtrude","CAP_FACE",FACE,{"disambiguationData":[OSD([sQuery(id+"F0.wireOp",EDGE,"E4"),sQuery(id+"F0.wireOp",EDGE,"E5.MirrorCS"),sQuery(id+"F0.wireOp",EDGE,"E7"),sQuery(id+"F0.wireOp",EDGE,"E8"),sQuery(id+"F0.wireOp",EDGE,"E9"),sQuery(id+"F0.wireOp",EDGE,"E10.1.1"),sQuery(id+"F0.wireOp",EDGE,"E10.1.3"),sQuery(id+"F0.wireOp",EDGE,"E10.1.7"),sQuery(id+"F0.wireOp",EDGE,"E10.1.8"),sQuery(id+"F0.wireOp",EDGE,"E10.2.1"),sQuery(id+"F0.wireOp",EDGE,"E10.2.3"),sQuery(id+"F0.wireOp",EDGE,"E10.2.7"),sQuery(id+"F0.wireOp",EDGE,"E10.2.8"),sQuery(id+"F0.wireOp",EDGE,"E10.3.1"),sQuery(id+"F0.wireOp",EDGE,"E10.3.3"),sQuery(id+"F0.wireOp",EDGE,"E10.3.7"),sQuery(id+"F0.wireOp",EDGE,"E10.3.8"),sQuery(id+"F0.wireOp",EDGE,"E10.4.1"),sQuery(id+"F0.wireOp",EDGE,"E10.4.3"),sQuery(id+"F0.wireOp",EDGE,"E10.4.7"),sQuery(id+"F0.wireOp",EDGE,"E10.4.8"),sQuery(id+"F0.wireOp",EDGE,"E10.5.1"),sQuery(id+"F0.wireOp",EDGE,"E10.5.3"),sQuery(id+"F0.wireOp",EDGE,"E10.5.7"),sQuery(id+"F0.wireOp",EDGE,"E10.5.8"),sQuery(id+"F0.wireOp",EDGE,"E10.6.1"),sQuery(id+"F0.wireOp",EDGE,"E10.6.3"),sQuery(id+"F0.wireOp",EDGE,"E10.6.7"),sQuery(id+"F0.wireOp",EDGE,"E10.6.8"),sQuery(id+"F0.wireOp",EDGE,"E10.7.1"),sQuery(id+"F0.wireOp",EDGE,"E10.7.3"),sQuery(id+"F0.wireOp",EDGE,"E10.7.7"),sQuery(id+"F0.wireOp",EDGE,"E10.7.8"),sQuery(id+"F0.wireOp",EDGE,"E10.8.1"),sQuery(id+"F0.wireOp",EDGE,"E10.8.3"),sQuery(id+"F0.wireOp",EDGE,"E10.8.7"),sQuery(id+"F0.wireOp",EDGE,"E10.8.8"),sQuery(id+"F0.wireOp",EDGE,"E10.9.1"),sQuery(id+"F0.wireOp",EDGE,"E10.9.3"),sQuery(id+"F0.wireOp",EDGE,"E10.9.7"),sQuery(id+"F0.wireOp",EDGE,"E10.9.8"),sQuery(id+"F0.wireOp",EDGE,"E10.10.1"),sQuery(id+"F0.wireOp",EDGE,"E10.10.3"),sQuery(id+"F0.wireOp",EDGE,"E10.10.7"),sQuery(id+"F0.wireOp",EDGE,"E10.10.8"),sQuery(id+"F0.wireOp",EDGE,"E10.11.1"),sQuery(id+"F0.wireOp",EDGE,"E10.11.3"),sQuery(id+"F0.wireOp",EDGE,"E10.11.7"),sQuery(id+"F0.wireOp",EDGE,"E10.11.8")])],"isStart":false});
            var sketch = newSketch(context, id + "F4", { "sketchPlane" : qUnion([Q0])});
            skCircle(sketch, "E22", {"center": v(0, 0) * mm, "radius": 4.34 * mm});
            skSolve(sketch);
        }
        {
            var Q0;
            Q0 = qSketchRegion(id + "F4", true);
            extrude(context, id + "F5", {"entities" : qUnion([Q0]), "operationType" : NewBodyOperationType.REMOVE, "oppositeDirection" : true, "depth" : 25 * mm});
        }
    });
